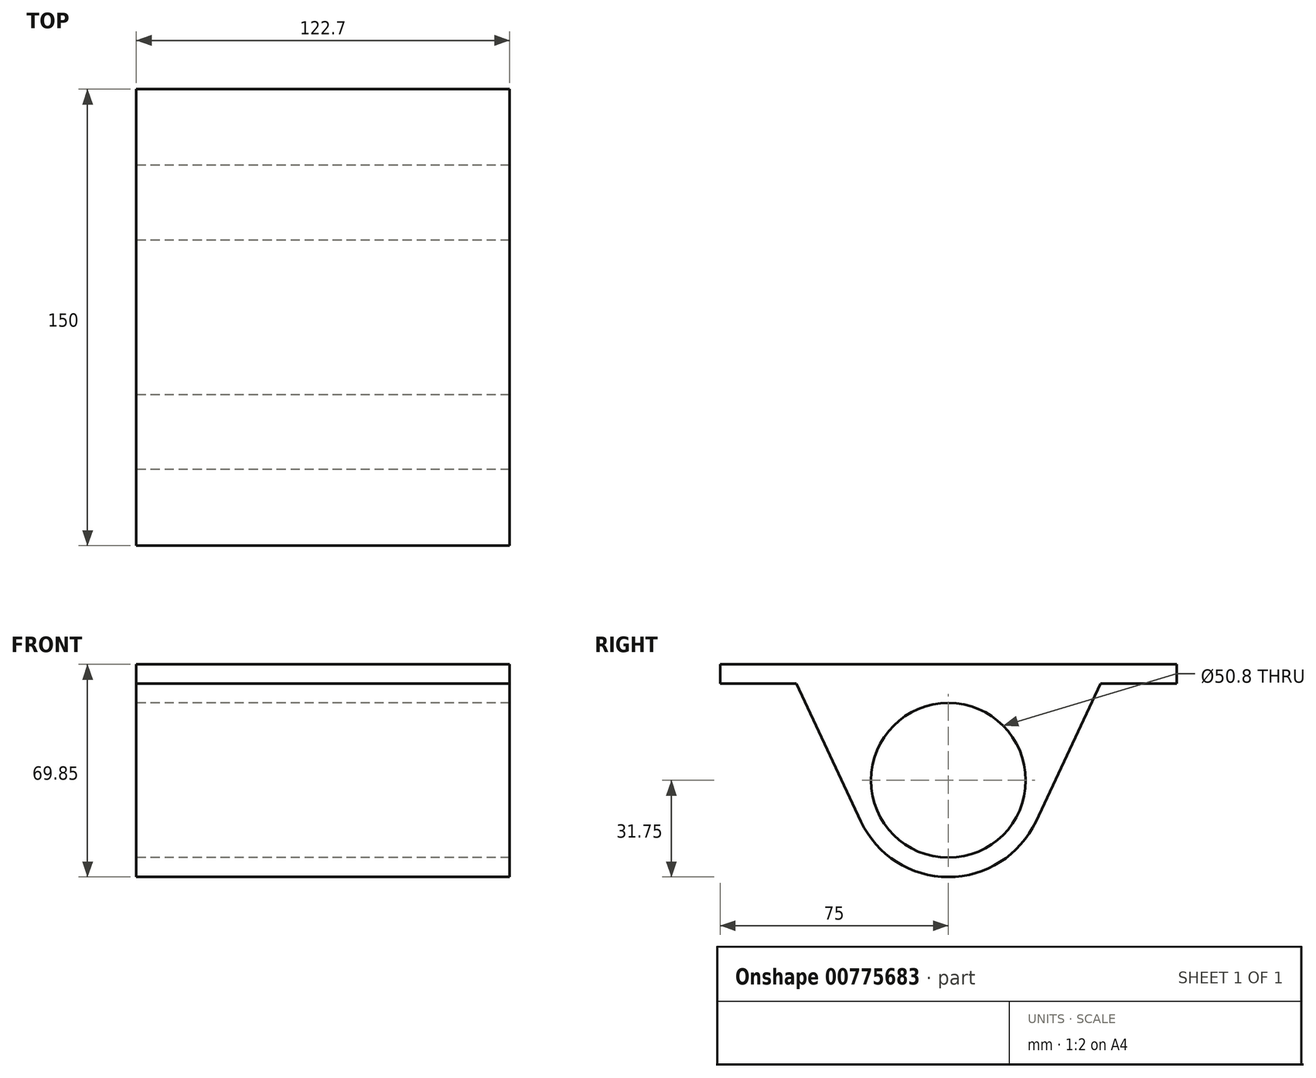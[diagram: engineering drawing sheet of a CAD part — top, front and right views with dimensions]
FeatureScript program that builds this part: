
annotation { "Feature Type Name" : "Feature", "Feature Type Description" : "" }
export const myFeature = defineFeature(function(context is Context, id is Id, definition is map)
    precondition{}
    {
        {
            var Q0;
            Q0=qCreatedBy(makeId("Right.planeOp"),FACE);
            var sketch = newSketch(context, id + "F0", { "sketchPlane" : qUnion([Q0])});
            skCircle(sketch, "E0", {"center": v(0, 0) * mm, "radius": 25.4 * mm});
            skLineSegment(sketch, "E1.bottom", {"start": v(-75, 38.1) * mm, "end": v(75, 38.1) * mm});
            skLineSegment(sketch, "E1.top", {"start": v(-75, 31.75) * mm, "end": v(75, 31.75) * mm});
            skLineSegment(sketch, "E1.left", {"start": v(-75, 38.1) * mm, "end": v(-75, 31.75) * mm});
            skLineSegment(sketch, "E1.right", {"start": v(75, 38.1) * mm, "end": v(75, 31.75) * mm});
            skCircle(sketch, "E2", {"center": v(0, 0) * mm, "radius": 31.75 * mm});
            skLineSegment(sketch, "E3", {"start": v(50, 31.75) * mm, "end": v(28.74, -13.5) * mm});
            skLineSegment(sketch, "E4", {"start": v(-50, 31.75) * mm, "end": v(-28.74, -13.5) * mm});
            skSolve(sketch);
        }
        {
            var Q0;
            Q0=makeQuery(id+"F0.imprint","IMPRINT",FACE,{"disambiguationData":[TD([[makeQuery(id+"F0.imprint","IMPRINT",EDGE,{"derivedFrom":sQuery(id+"F0.wireOp",EDGE,"E1.bottom")}),-1.0]])]});
            var Q1;
            {var subQ0=sQuery(id+"F0.wireOp",EDGE,"E4");Q1=makeQuery(id+"F0.imprint","IMPRINT",FACE,{"disambiguationData":[TD([[makeQuery(id+"F0.imprint","IMPRINT",EDGE,{"derivedFrom":subQ0}),1.0]])]});}
            var Q2;
            Q2=makeQuery(id+"F0.imprint","IMPRINT",FACE,{"disambiguationData":[TD([[makeQuery(id+"F0.imprint","IMPRINT",EDGE,{"derivedFrom":sQuery(id+"F0.wireOp",EDGE,"E0")}),-1.0]])]});
            var Q3;
            {var subQ0=sQuery(id+"F0.wireOp",EDGE,"E3");Q3=makeQuery(id+"F0.imprint","IMPRINT",FACE,{"disambiguationData":[TD([[makeQuery(id+"F0.imprint","IMPRINT",EDGE,{"derivedFrom":subQ0}),-1.0]])]});}
            extrude(context, id + "F1", {"entities" : qUnion([Q0, Q1, Q2, Q3]), "depth" : 122.7 * mm, "offsetDistance" : 25 * mm, "symmetric" : true});
        }
    });
